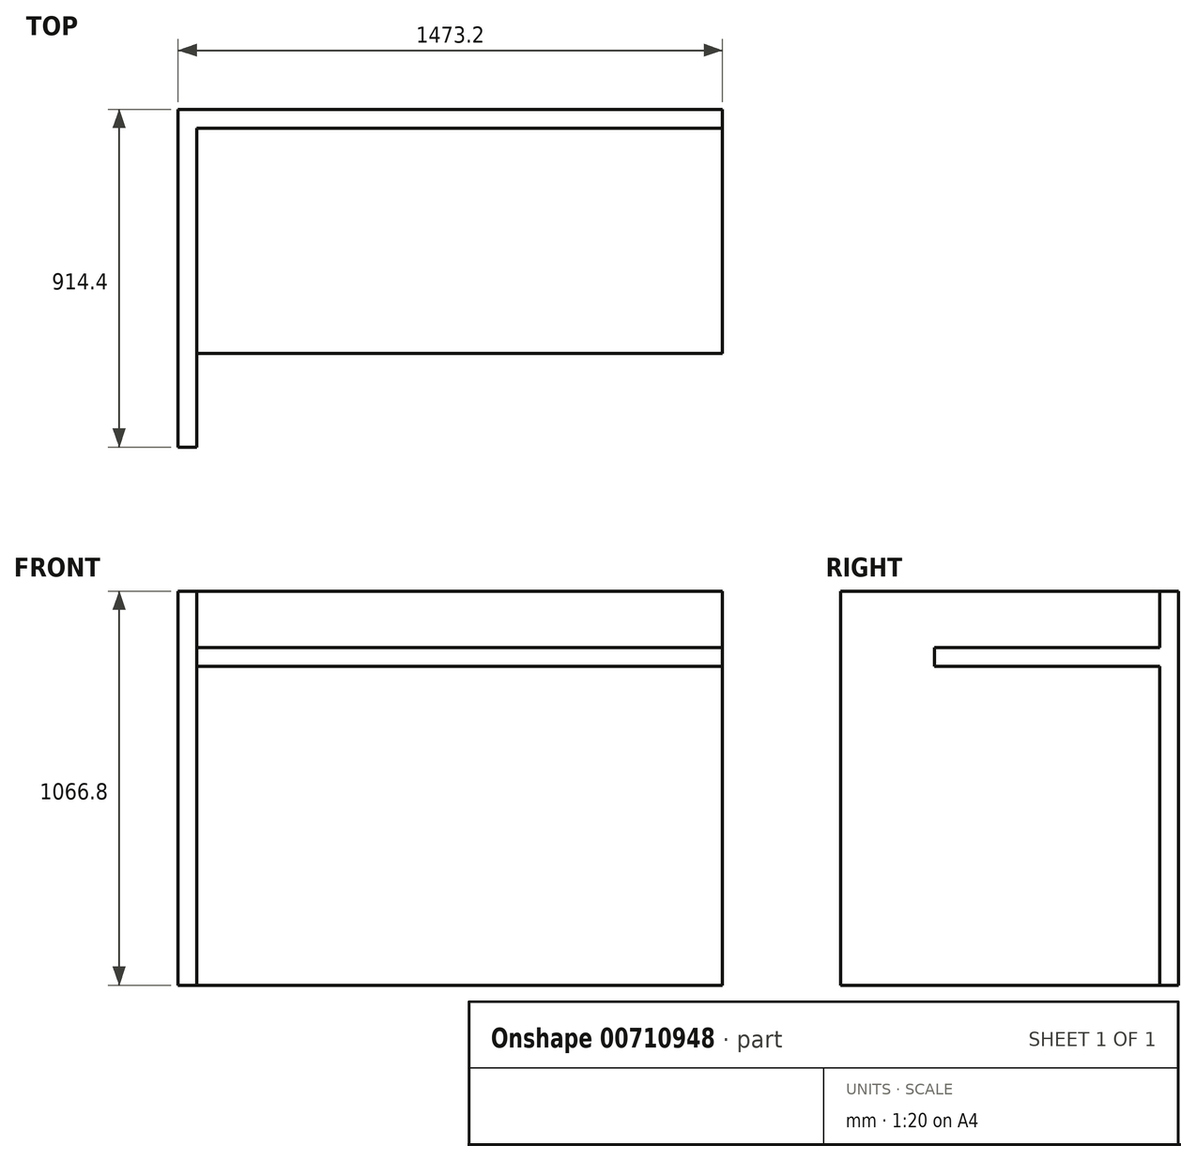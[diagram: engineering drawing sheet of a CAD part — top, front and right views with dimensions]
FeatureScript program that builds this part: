
annotation { "Feature Type Name" : "Feature", "Feature Type Description" : "" }
export const myFeature = defineFeature(function(context is Context, id is Id, definition is map)
    precondition{}
    {
        {
            var Q0;
            Q0=qCreatedBy(makeId("Top.planeOp"),FACE);
            var sketch = newSketch(context, id + "F0", { "sketchPlane" : qUnion([Q0])});
            skLineSegment(sketch, "E0.bottom", {"start": v(-736.6, 457.2) * mm, "end": v(736.6, 457.2) * mm});
            skLineSegment(sketch, "E0.top", {"start": v(-736.6, -457.2) * mm, "end": v(736.6, -457.2) * mm});
            skLineSegment(sketch, "E0.left", {"start": v(-736.6, 457.2) * mm, "end": v(-736.6, -457.2) * mm});
            skLineSegment(sketch, "E0.right", {"start": v(736.6, 457.2) * mm, "end": v(736.6, -457.2) * mm});
            skLineSegment(sketch, "E1", {"start": v(0, 0) * mm, "end": v(0, 457.2) * mm, "construction": true});
            skLineSegment(sketch, "E2", {"start": v(0, 0) * mm, "end": v(-736.6, 0) * mm, "construction": true});
            skSolve(sketch);
        }
        {
            var Q0;
            Q0 = qSketchRegion(id + "F0", true);
            extrude(context, id + "F1", {"entities" : qUnion([Q0]), "depth" : 1066.8 * mm, "offsetDistance" : 25.4 * mm});
        }
        {
            var Q0;
            Q0=makeQuery(id+"F1.opExtrude","CAP_FACE",FACE,{"disambiguationData":[OSD([sQuery(id+"F0.wireOp",EDGE,"E0.bottom"),sQuery(id+"F0.wireOp",EDGE,"E0.top"),sQuery(id+"F0.wireOp",EDGE,"E0.left"),sQuery(id+"F0.wireOp",EDGE,"E0.right")])],"isStart":false});
            var sketch = newSketch(context, id + "F2", { "sketchPlane" : qUnion([Q0])});
            skLineSegment(sketch, "E3.bottom", {"start": v(736.6, -457.2) * mm, "end": v(-685.8, -457.2) * mm});
            skLineSegment(sketch, "E3.top", {"start": v(736.6, 406.4) * mm, "end": v(-685.8, 406.4) * mm});
            skLineSegment(sketch, "E3.left", {"start": v(736.6, -457.2) * mm, "end": v(736.6, 406.4) * mm});
            skLineSegment(sketch, "E3.right", {"start": v(-685.8, -457.2) * mm, "end": v(-685.8, 406.4) * mm});
            skSolve(sketch);
        }
        {
            var Q0;
            Q0 = qSketchRegion(id + "F2", true);
            extrude(context, id + "F3", {"entities" : qUnion([Q0]), "operationType" : NewBodyOperationType.REMOVE, "oppositeDirection" : true, "depth" : 152.4 * mm, "offsetDistance" : 25.4 * mm});
        }
        {
            var Q0;
            Q0=makeQuery(id+"F1.opExtrude","CAP_FACE",FACE,{"disambiguationData":[OSD([sQuery(id+"F0.wireOp",EDGE,"E0.bottom"),sQuery(id+"F0.wireOp",EDGE,"E0.top"),sQuery(id+"F0.wireOp",EDGE,"E0.left"),sQuery(id+"F0.wireOp",EDGE,"E0.right")])],"isStart":true});
            var sketch = newSketch(context, id + "F4", { "sketchPlane" : qUnion([Q0])});
            skLineSegment(sketch, "E4.bottom", {"start": v(736.6, 457.2) * mm, "end": v(-685.8, 457.2) * mm});
            skLineSegment(sketch, "E4.top", {"start": v(736.6, -406.4) * mm, "end": v(-685.8, -406.4) * mm});
            skLineSegment(sketch, "E4.left", {"start": v(736.6, 457.2) * mm, "end": v(736.6, -406.4) * mm});
            skLineSegment(sketch, "E4.right", {"start": v(-685.8, 457.2) * mm, "end": v(-685.8, -406.4) * mm});
            skSolve(sketch);
        }
        {
            var Q0;
            Q0 = qSketchRegion(id + "F4", true);
            extrude(context, id + "F5", {"entities" : qUnion([Q0]), "operationType" : NewBodyOperationType.REMOVE, "oppositeDirection" : true, "depth" : 863.6 * mm, "offsetDistance" : 25.4 * mm});
        }
        {
            var Q0;
            Q0=makeQuery(id+"F3.boolean.opBoolean","COPY",FACE,{"derivedFrom":makeQuery(id+"F3.opExtrude","CAP_FACE",FACE,{"disambiguationData":[OSD([sQuery(id+"F2.wireOp",EDGE,"E3.bottom"),sQuery(id+"F2.wireOp",EDGE,"E3.top"),sQuery(id+"F2.wireOp",EDGE,"E3.left"),sQuery(id+"F2.wireOp",EDGE,"E3.right")])],"isStart":false})});
            var sketch = newSketch(context, id + "F6", { "sketchPlane" : qUnion([Q0])});
            skLineSegment(sketch, "E5.bottom", {"start": v(736.6, -457.2) * mm, "end": v(-685.8, -457.2) * mm});
            skLineSegment(sketch, "E5.top", {"start": v(736.6, -203.2) * mm, "end": v(-685.8, -203.2) * mm});
            skLineSegment(sketch, "E5.left", {"start": v(736.6, -457.2) * mm, "end": v(736.6, -203.2) * mm});
            skLineSegment(sketch, "E5.right", {"start": v(-685.8, -457.2) * mm, "end": v(-685.8, -203.2) * mm});
            skSolve(sketch);
        }
        {
            var Q0;
            Q0 = qSketchRegion(id + "F6", true);
            extrude(context, id + "F7", {"entities" : qUnion([Q0]), "operationType" : NewBodyOperationType.REMOVE, "endBound" : BoundingType.THROUGH_ALL, "oppositeDirection" : true, "depth" : 25.4 * mm, "offsetDistance" : 25.4 * mm});
        }
    });
